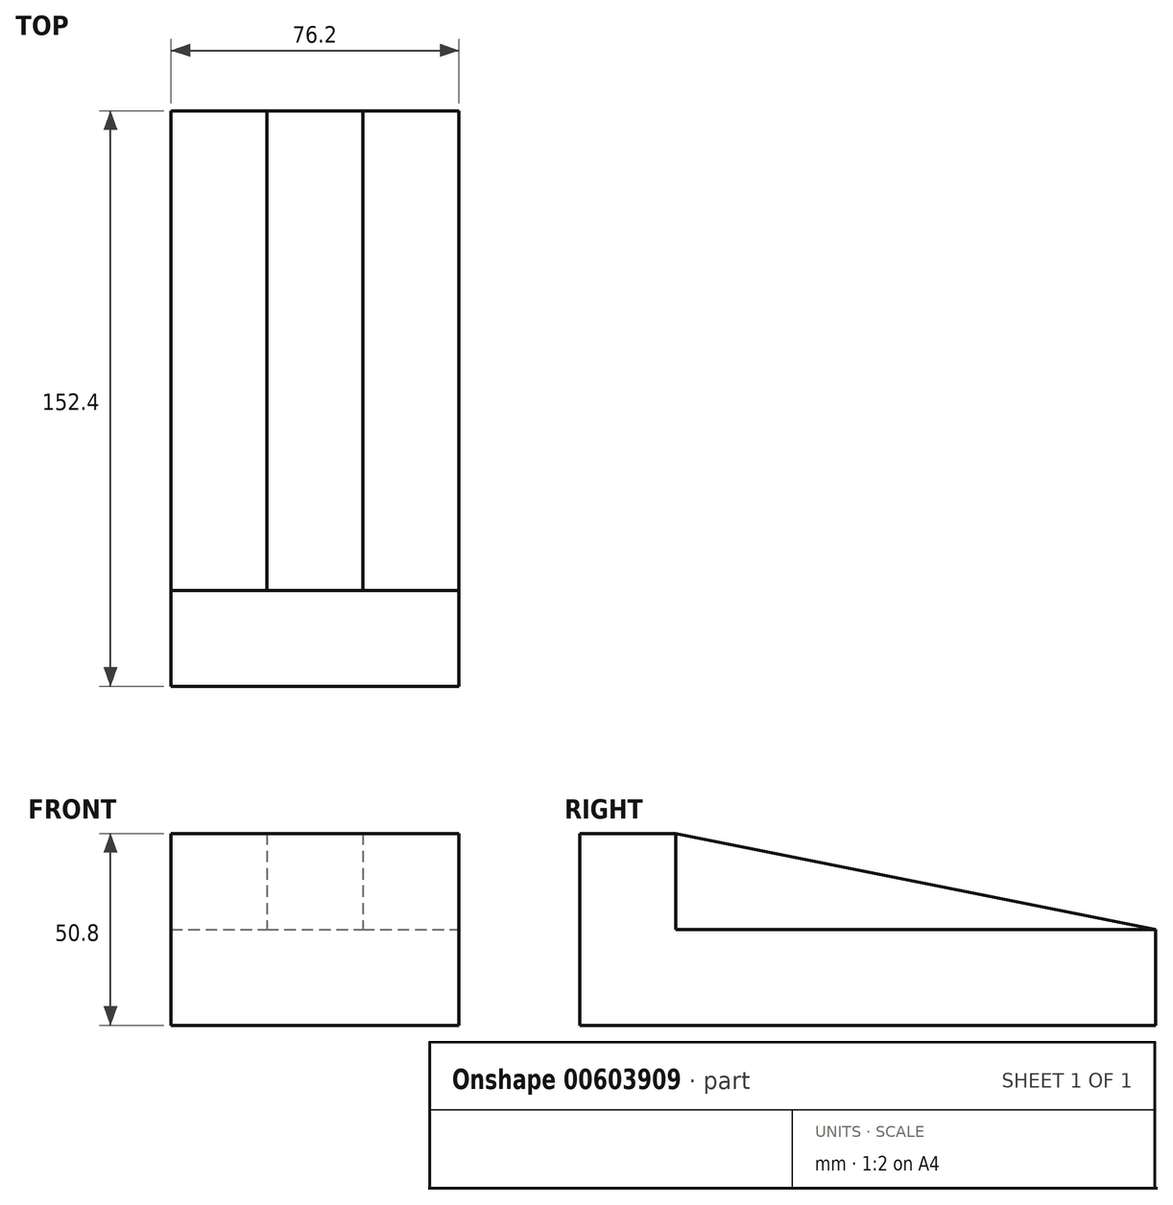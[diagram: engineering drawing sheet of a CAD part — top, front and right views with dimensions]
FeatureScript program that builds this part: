
annotation { "Feature Type Name" : "Feature", "Feature Type Description" : "" }
export const myFeature = defineFeature(function(context is Context, id is Id, definition is map)
    precondition{}
    {
        {
            var Q0;
            Q0=qCreatedBy(makeId("Front.planeOp"),FACE);
            var sketch = newSketch(context, id + "F0", { "sketchPlane" : qUnion([Q0])});
            skLineSegment(sketch, "E0.bottom", {"start": v(0, 0) * mm, "end": v(76.2, 0) * mm});
            skLineSegment(sketch, "E0.top", {"start": v(0, 25.4) * mm, "end": v(76.2, 25.4) * mm});
            skLineSegment(sketch, "E0.left", {"start": v(0, 0) * mm, "end": v(0, 25.4) * mm});
            skLineSegment(sketch, "E0.right", {"start": v(76.2, 0) * mm, "end": v(76.2, 25.4) * mm});
            skSolve(sketch);
        }
        {
            var Q0;
            Q0=makeQuery(id+"F0.imprint","IMPRINT",FACE,{"disambiguationData":[TD([[makeQuery(id+"F0.imprint","IMPRINT",EDGE,{"derivedFrom":sQuery(id+"F0.wireOp",EDGE,"E0.bottom")}),1.0]])]});
            extrude(context, id + "F1", {"entities" : qUnion([Q0]), "oppositeDirection" : true, "depth" : 152.4 * mm, "offsetDistance" : 25.4 * mm});
        }
        {
            var Q0;
            Q0=makeQuery(id+"F1.opExtrude","SWEPT_FACE",FACE,{"disambiguationData":[OSD([sQuery(id+"F0.wireOp",EDGE,"E0.top")])]});
            var sketch = newSketch(context, id + "F2", { "sketchPlane" : qUnion([Q0])});
            skLineSegment(sketch, "E1.bottom", {"start": v(0, 0) * mm, "end": v(76.2, 0) * mm});
            skLineSegment(sketch, "E1.top", {"start": v(0, 25.4) * mm, "end": v(76.2, 25.4) * mm});
            skLineSegment(sketch, "E1.left", {"start": v(0, 0) * mm, "end": v(0, 25.4) * mm});
            skLineSegment(sketch, "E1.right", {"start": v(76.2, 0) * mm, "end": v(76.2, 25.4) * mm});
            skLineSegment(sketch, "E2.bottom", {"start": v(25.4, 152.4) * mm, "end": v(50.8, 152.4) * mm});
            skLineSegment(sketch, "E2.top", {"start": v(25.4, 25.4) * mm, "end": v(50.8, 25.4) * mm});
            skLineSegment(sketch, "E2.left", {"start": v(25.4, 152.4) * mm, "end": v(25.4, 25.4) * mm});
            skLineSegment(sketch, "E2.right", {"start": v(50.8, 152.4) * mm, "end": v(50.8, 25.4) * mm});
            skSolve(sketch);
        }
        {
            var Q0;
            Q0=makeQuery(id+"F2.imprint","IMPRINT",FACE,{"disambiguationData":[TD([[makeQuery(id+"F2.imprint","IMPRINT",EDGE,{"derivedFrom":sQuery(id+"F2.wireOp",EDGE,"E1.bottom")}),1.0]])]});
            var Q1;
            Q1=makeQuery(id+"F2.imprint","IMPRINT",FACE,{"disambiguationData":[TD([[makeQuery(id+"F2.imprint","IMPRINT",EDGE,{"derivedFrom":sQuery(id+"F2.wireOp",EDGE,"E2.bottom")}),-1.0]])]});
            extrude(context, id + "F3", {"entities" : qUnion([Q0, Q1]), "operationType" : NewBodyOperationType.ADD, "depth" : 25.4 * mm, "offsetDistance" : 25.4 * mm});
        }
        {
            var Q0;
            Q0=makeQuery(id+"F3.opExtrude","SWEPT_FACE",FACE,{"disambiguationData":[OSD([sQuery(id+"F2.wireOp",EDGE,"E2.right")])]});
            var sketch = newSketch(context, id + "F4", { "sketchPlane" : qUnion([Q0])});
            skLineSegment(sketch, "E3", {"start": v(25.4, 50.8) * mm, "end": v(152.4, 25.4) * mm});
            skSolve(sketch);
        }
        {
            var Q0;
            Q0=makeQuery(id+"F4.imprint","IMPRINT",FACE,{"disambiguationData":[TD([[makeQuery(id+"F4.imprint","IMPRINT",EDGE,{"derivedFrom":sQuery(id+"F4.wireOp",EDGE,"E3")}),1.0]])]});
            extrude(context, id + "F5", {"entities" : qUnion([Q0]), "operationType" : NewBodyOperationType.REMOVE, "oppositeDirection" : true, "depth" : 25.4 * mm, "offsetDistance" : 25.4 * mm});
        }
    });
